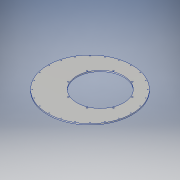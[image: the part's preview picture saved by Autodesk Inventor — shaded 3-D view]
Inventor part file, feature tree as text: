
AUTODESK INVENTOR PART (.ipt)
format: ipt  version: 2018 (Build 220112000, 112)  size: 160,768 bytes
history: native  units: in
note: dims shown in document units (in); Inventor stores cm internally (conversion verified against a paired STEP export)
features: sketch x4, extrude x2, hole x2, pattern_circular x2
ambient origin geometry x8: Origin, YZ Plane, XZ Plane, XY Plane, X Axis, Y Axis, Z Axis, Center Point
bodies: Solid1 (feature_tree)
feature tree (10):
  extrude  "Extrusion1"  Depth=0.25in TaperAngle=0.0deg
  hole  "Hole3"  [1 undecoded]
  pattern_circular  "Circular Pattern1"  Angle=45.0deg  [1 undecoded]
  extrude  "Extrusion4"  Depth=0.25in
  hole  "Hole4"  [1 undecoded]
  pattern_circular  "Circular Pattern2"  [2 undecoded]
  sketch  "Sketch1"  dims[d0=18.0in d1=0.25in d2=0.0in]
  sketch  "Sketch7"  dims[d42=8.75in]
  sketch  "Sketch8"  dims[d43=0.13in d44=0.328in d45=0.375in d46=0.25in d47=0.5635in d48=0.484in d49=0.8108in d50=9.4488in d51=360.0deg]
  sketch  "Sketch9"  dims[d53=1.56in d54=45.0deg d55=10.0in d56=1.0in d57=0.0in d58=5.25in d59=22.5deg d60=0.266in d61=0.5in d62=0.507in d63=0.25in d64=0.5635in d65=1.0in d66=0.8108in d67=3.1496in d68=360.0deg]
note: 5 required parameter values undecoded (feature->parameter linkage not recoverable at this tier; creation-order binding heuristic only, values carry confidence <= 0.55)
